# Revit family: GR_Адаптер линейный_Муфта(n)_Airslot-КСД-У_О_R21
name_source: partatom
category: Соединительные детали воздуховодов
units: mm (PartAtom-declared; Revit-internal decimal feet)

## family parameters
Всегда вертикально = Да
Заголовок OmniClass = Metal Ducts
На основе рабочей плоскости = Нет
Номер OmniClass = 23.75.70.14.31
Общий = Нет
При загрузке вырезать с полостями = Нет
Размер круглого соединителя = Использовать диаметр
Тип детали = Мультипорт

## types (18) — shared parameters
ADSK_URL страницы изделия = https://grilles.ru
ADSK_Версия Revit = 2021
ADSK_Единица измерения = шт.
ADSK_Завод-изготовитель = ООО "ВЕНТРЕШЕТКИКОМ"
ADSK_Код изделия = 000003
ADSK_Количество = 1
ADSK_Материал = ADSK_Оцинкованная сталь
ADSK_Наименование = Airslot-КСД-У-О, адаптер вентиляционной решётки радиальный
Изготовитель = ООО "ВЕНТРЕШЕТКИКОМ"
Корпус_Металл_Толщина = 1 мм
Муфта_Металл_Толщина = 1 мм
zero-valued in all types: Отметка по умолчанию

## per-type parameters (varying)
| type | Корпус_Высота | Корпус_Длина | Решетка_отступ | Решётка_Высота |
| Airslot-КСД-У-О 1-20 | 130 мм | 218 мм | 25 мм | 48 мм |
| Airslot-КСД-У-О 2-20 | 130 мм | 256 мм | 45 мм | 88 мм |
| Airslot-КСД-У-О 3-20 | 130 мм | 294 мм | 65 мм | 127 мм |
| Airslot-КСД-У-О 4-20 | 170 мм | 334 мм | 85 мм | 167 мм |
| Airslot-КСД-У-О 5-20 | 170 мм | 372 мм | 104 мм | 206 мм |
| Airslot-КСД-У-О 6-20 | 170 мм | 412 мм | 124 мм | 246 мм |
| Airslot-КСД-У-О 1-25 | 130 мм | 218 мм | 28 мм | 53 мм |
| Airslot-КСД-У-О 2-25 | 130 мм | 256 мм | 50 мм | 98 мм |
| Airslot-КСД-У-О 3-25 | 130 мм | 318 мм | 72 мм | 142 мм |
| Airslot-КСД-У-О 4-25 | 170 мм | 390 мм | 95 мм | 187 мм |
| Airslot-КСД-У-О 5-25 | 170 мм | 440 мм | 117 мм | 231 мм |
| Airslot-КСД-У-О 6-25 | 170 мм | 480 мм | 139 мм | 276 мм |
| Airslot-КСД-У-О 1-30 | 130 мм | 218 мм | 30 мм | 58 мм |
| Airslot-КСД-У-О 2-30 | 130 мм | 256 мм | 55 мм | 108 мм |
| Airslot-КСД-У-О 3-30 | 130 мм | 318 мм | 80 мм | 157 мм |
| Airslot-КСД-У-О 4-30 | 170 мм | 390 мм | 105 мм | 207 мм |
| Airslot-КСД-У-О 5-30 | 170 мм | 440 мм | 129 мм | 256 мм |
| Airslot-КСД-У-О 6-30 | 170 мм | 480 мм | 154 мм | 306 мм |

note: column(s) folded — value = type name in every type: ADSK_Марка
